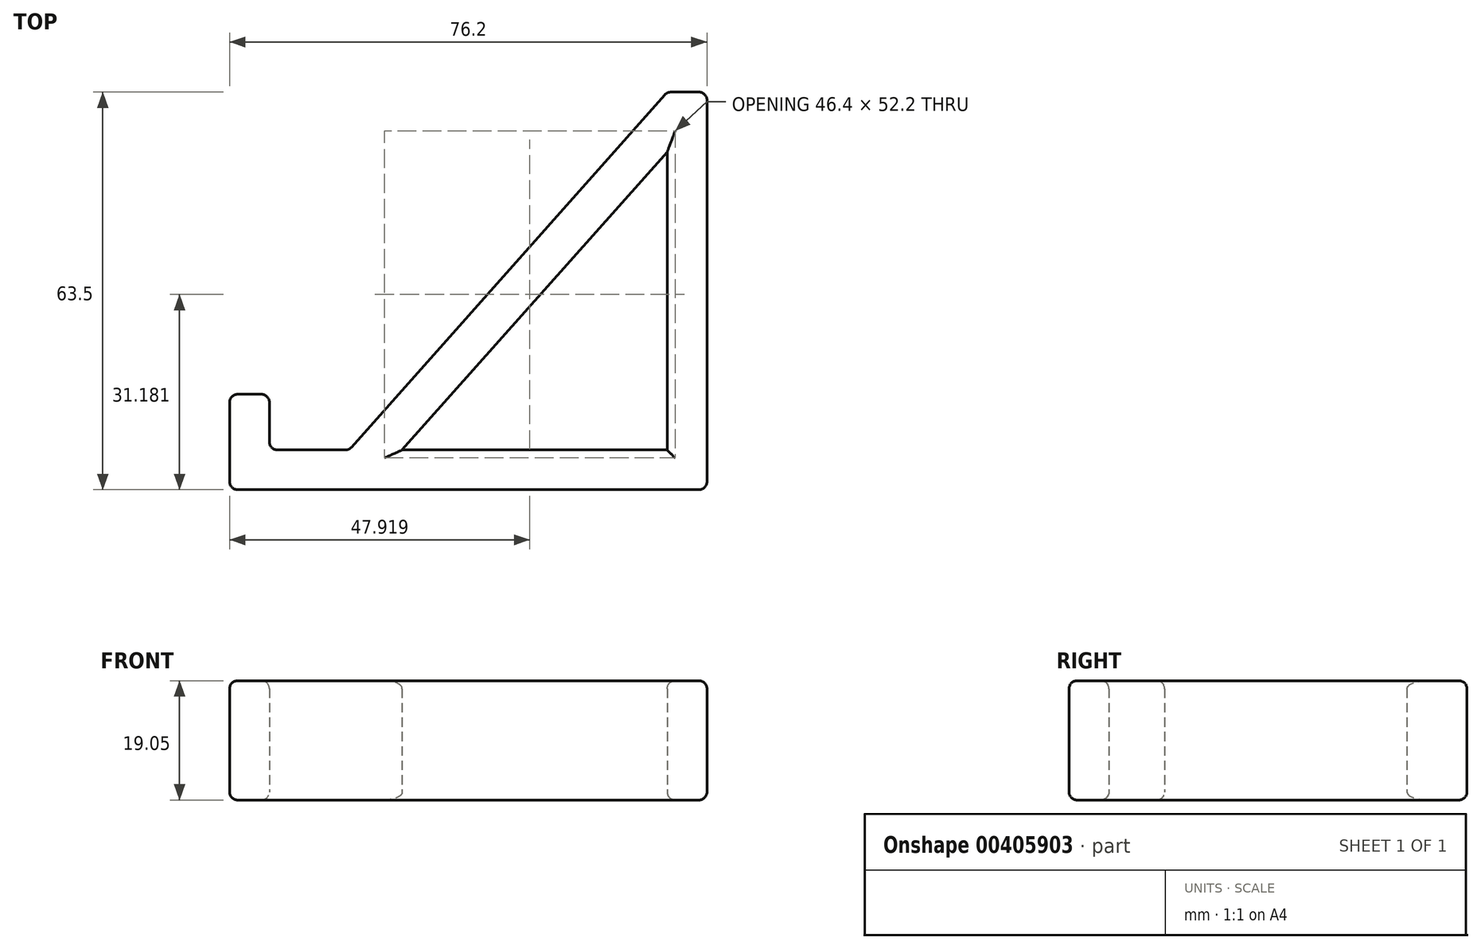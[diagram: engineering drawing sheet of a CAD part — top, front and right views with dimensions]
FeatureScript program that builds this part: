
annotation { "Feature Type Name" : "Feature", "Feature Type Description" : "" }
export const myFeature = defineFeature(function(context is Context, id is Id, definition is map)
    precondition{}
    {
        {
            var Q0;
            Q0=qCreatedBy(makeId("Top.planeOp"),FACE);
            var sketch = newSketch(context, id + "F0", { "sketchPlane" : qUnion([Q0])});
            skLineSegment(sketch, "E0", {"start": v(0, 0) * mm, "end": v(-76.2, 0) * mm});
            skLineSegment(sketch, "E1", {"start": v(-76.2, 0) * mm, "end": v(-76.2, 15.24) * mm});
            skLineSegment(sketch, "E2", {"start": v(-76.2, 15.24) * mm, "end": v(-69.85, 15.24) * mm});
            skLineSegment(sketch, "E3", {"start": v(-69.85, 15.24) * mm, "end": v(-69.85, 6.35) * mm});
            skLineSegment(sketch, "E4", {"start": v(-69.85, 6.35) * mm, "end": v(-57.15, 6.35) * mm});
            skLineSegment(sketch, "E5", {"start": v(0, 0) * mm, "end": v(0, 63.5) * mm});
            skLineSegment(sketch, "E6", {"start": v(0, 63.5) * mm, "end": v(-6.35, 63.5) * mm});
            skLineSegment(sketch, "E7", {"start": v(-6.35, 63.5) * mm, "end": v(-57.15, 6.35) * mm});
            skLineSegment(sketch, "E8", {"start": v(-57.15, 6.35) * mm, "end": v(49.33, 6.35) * mm, "construction": true});
            skLineSegment(sketch, "E9", {"start": v(-48.65, 6.35) * mm, "end": v(-6.35, 53.94) * mm});
            skLineSegment(sketch, "E10", {"start": v(-6.35, 53.94) * mm, "end": v(-6.35, 6.35) * mm});
            skLineSegment(sketch, "E11", {"start": v(-6.35, 6.35) * mm, "end": v(-48.65, 6.35) * mm});
            skSolve(sketch);
        }
        {
            var Q0;
            Q0 = qSketchRegion(id + "F0", true);
            extrude(context, id + "F1", {"entities" : qUnion([Q0]), "depth" : 19.05 * mm});
        }
        {
            var Q0;
            Q0=makeQuery(id+"F1.opExtrude","CAP_EDGE",EDGE,{"disambiguationData":[OSD([sQuery(id+"F0.wireOp",EDGE,"E7")])],"isStart":false});
            var Q1;
            Q1=makeQuery(id+"F1.opExtrude","CAP_FACE",FACE,{"disambiguationData":[OSD([sQuery(id+"F0.wireOp",EDGE,"E0"),sQuery(id+"F0.wireOp",EDGE,"E1"),sQuery(id+"F0.wireOp",EDGE,"E2"),sQuery(id+"F0.wireOp",EDGE,"E3"),sQuery(id+"F0.wireOp",EDGE,"E4"),sQuery(id+"F0.wireOp",EDGE,"E5"),sQuery(id+"F0.wireOp",EDGE,"E6"),sQuery(id+"F0.wireOp",EDGE,"E7"),sQuery(id+"F0.wireOp",EDGE,"E9"),sQuery(id+"F0.wireOp",EDGE,"E10"),sQuery(id+"F0.wireOp",EDGE,"E11")])],"isStart":false});
            var Q2;
            Q2=makeQuery(id+"F1.opExtrude","CAP_FACE",FACE,{"disambiguationData":[OSD([sQuery(id+"F0.wireOp",EDGE,"E0"),sQuery(id+"F0.wireOp",EDGE,"E1"),sQuery(id+"F0.wireOp",EDGE,"E2"),sQuery(id+"F0.wireOp",EDGE,"E3"),sQuery(id+"F0.wireOp",EDGE,"E4"),sQuery(id+"F0.wireOp",EDGE,"E5"),sQuery(id+"F0.wireOp",EDGE,"E6"),sQuery(id+"F0.wireOp",EDGE,"E7"),sQuery(id+"F0.wireOp",EDGE,"E9"),sQuery(id+"F0.wireOp",EDGE,"E10"),sQuery(id+"F0.wireOp",EDGE,"E11")])],"isStart":true});
            var Q3;
            Q3=makeQuery(id+"F1.opExtrude","SWEPT_FACE",FACE,{"disambiguationData":[OSD([sQuery(id+"F0.wireOp",EDGE,"E3")])]});
            var Q4;
            Q4=makeQuery(id+"F1.opExtrude","SWEPT_EDGE",EDGE,{"disambiguationData":[OSD([sQuery(id+"F0.wireOp",EDGE,"E1"),sQuery(id+"F0.wireOp",EDGE,"E2")])]});
            var Q5;
            Q5=makeQuery(id+"F1.opExtrude","SWEPT_EDGE",EDGE,{"disambiguationData":[OSD([sQuery(id+"F0.wireOp",EDGE,"E0"),sQuery(id+"F0.wireOp",EDGE,"E5")])]});
            var Q6;
            Q6=makeQuery(id+"F1.opExtrude","SWEPT_EDGE",EDGE,{"disambiguationData":[OSD([sQuery(id+"F0.wireOp",EDGE,"E5"),sQuery(id+"F0.wireOp",EDGE,"E6")])]});
            var Q7;
            Q7=makeQuery(id+"F1.opExtrude","SWEPT_EDGE",EDGE,{"disambiguationData":[OSD([sQuery(id+"F0.wireOp",EDGE,"E6"),sQuery(id+"F0.wireOp",EDGE,"E7")])]});
            var Q8;
            Q8=makeQuery(id+"F1.opExtrude","SWEPT_EDGE",EDGE,{"disambiguationData":[OSD([sQuery(id+"F0.wireOp",EDGE,"E4"),sQuery(id+"F0.wireOp",EDGE,"E7")])]});
            var Q9;
            Q9=makeQuery(id+"F1.opExtrude","SWEPT_FACE",FACE,{"disambiguationData":[OSD([sQuery(id+"F0.wireOp",EDGE,"E1")])]});
            fillet(context, id + "F2", {"entities" : qUnion([Q0, Q1, Q2, Q3, Q4, Q5, Q6, Q7, Q8, Q9]), "radius" : 1.27 * mm, "tangentPropagation" : true, "allowEdgeOverflow" : false});
        }
    });
